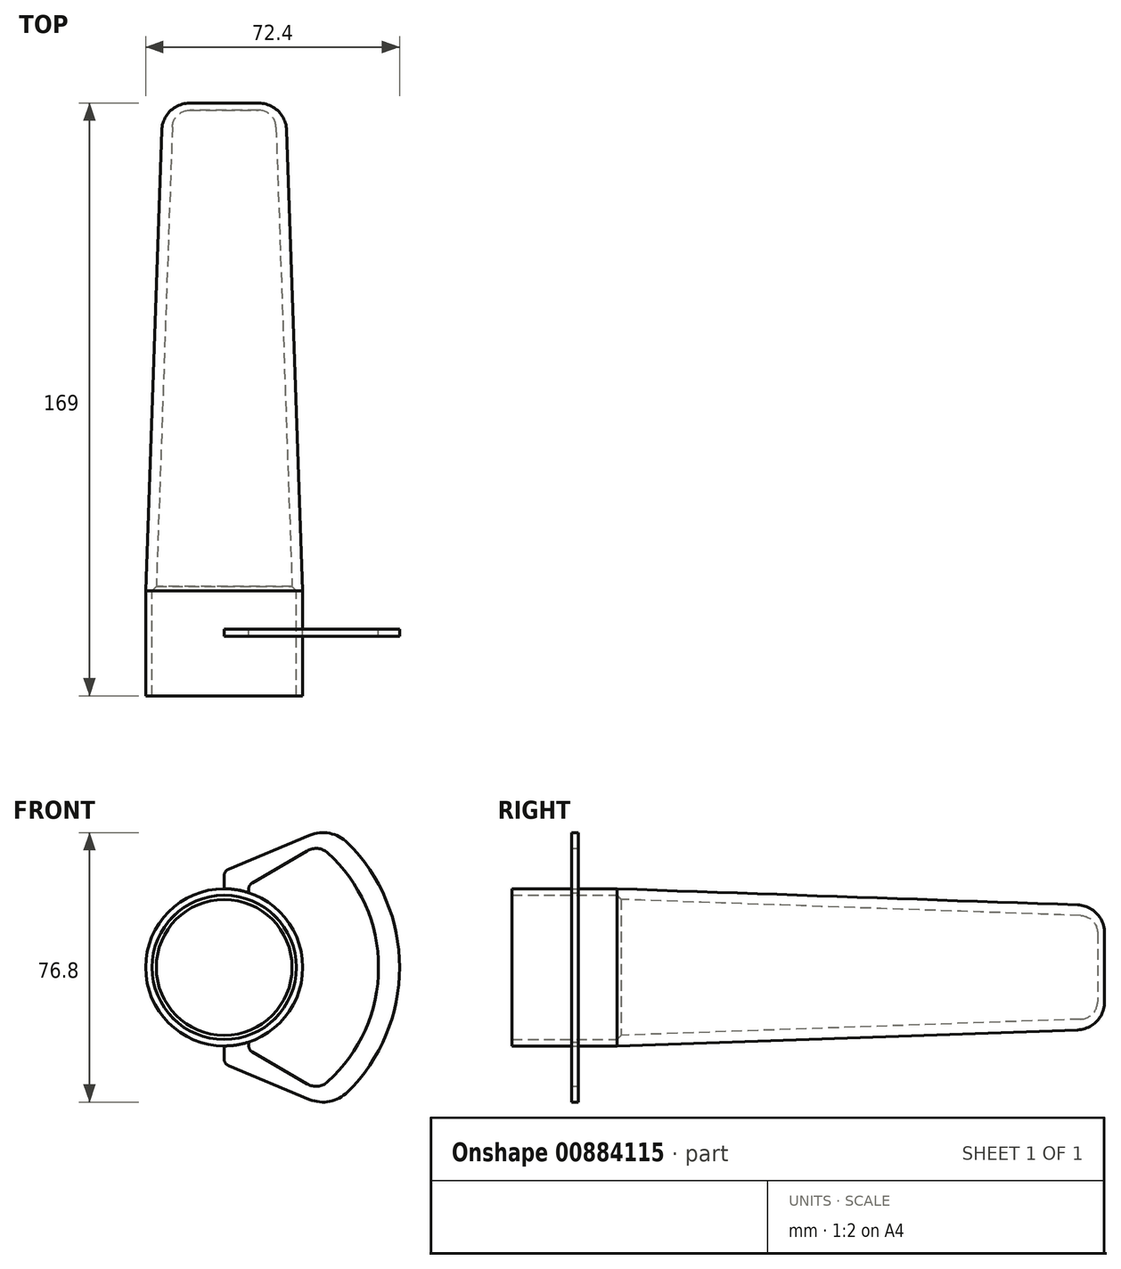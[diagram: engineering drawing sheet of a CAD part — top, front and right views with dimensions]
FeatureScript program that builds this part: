
annotation { "Feature Type Name" : "Feature", "Feature Type Description" : "" }
export const myFeature = defineFeature(function(context is Context, id is Id, definition is map)
    precondition{}
    {
        {
            var Q0;
            Q0=qCreatedBy(makeId("Front.planeOp"),FACE);
            var sketch = newSketch(context, id + "F0", { "sketchPlane" : qUnion([Q0])});
            skCircle(sketch, "E0", {"center": v(-13.8, 50.8) * mm, "radius": 22.4 * mm});
            skCircle(sketch, "E1", {"center": v(-13.8, 50.8) * mm, "radius": 20.57 * mm});
            skLineSegment(sketch, "E2", {"start": v(-12.57, 22.79) * mm, "end": v(10.52, 13.17) * mm});
            skLineSegment(sketch, "E3", {"start": v(-12.57, 78.81) * mm, "end": v(10.52, 88.43) * mm});
            skLineSegment(sketch, "E4", {"start": v(9.84, 17.57) * mm, "end": v(-5.8, 26.72) * mm});
            skLineSegment(sketch, "E5", {"start": v(-5.8, 74.88) * mm, "end": v(9.84, 84.03) * mm});
            skArc(sketch, "E6", {"start": v(21.4, 15.3) * mm, "mid": v(36.2, 50.8) * mm, "end": v(21.4, 86.3) * mm});
            skArc(sketch, "E7", {"start": v(15.72, 18.17) * mm, "mid": v(30.2, 50.8) * mm, "end": v(15.72, 83.42) * mm});
            skLineSegment(sketch, "E8", {"start": v(-13.8, 73.2) * mm, "end": v(-13.8, 76.97) * mm});
            skLineSegment(sketch, "E9", {"start": v(-6.8, 73.15) * mm, "end": v(-6.8, 72.08) * mm});
            skLineSegment(sketch, "E10", {"start": v(-6.8, 29.52) * mm, "end": v(-6.8, 28.45) * mm});
            skLineSegment(sketch, "E11", {"start": v(-13.8, 24.63) * mm, "end": v(-13.8, 28.4) * mm});
            skArc(sketch, "E12", {"start": v(15.72, 83.42) * mm, "mid": v(12.88, 84.69) * mm, "end": v(9.84, 84.03) * mm});
            skArc(sketch, "E13", {"start": v(9.84, 17.57) * mm, "mid": v(12.88, 16.9) * mm, "end": v(15.72, 18.17) * mm});
            skArc(sketch, "E14", {"start": v(21.4, 86.3) * mm, "mid": v(16.29, 89.02) * mm, "end": v(10.52, 88.43) * mm});
            skArc(sketch, "E15", {"start": v(10.52, 13.17) * mm, "mid": v(16.29, 12.58) * mm, "end": v(21.4, 15.3) * mm});
            skArc(sketch, "E16", {"start": v(-6.8, 28.45) * mm, "mid": v(-6.53, 27.45) * mm, "end": v(-5.8, 26.72) * mm});
            skArc(sketch, "E17", {"start": v(-13.8, 24.63) * mm, "mid": v(-13.46, 23.52) * mm, "end": v(-12.57, 22.79) * mm});
            skArc(sketch, "E18", {"start": v(-12.57, 78.81) * mm, "mid": v(-13.46, 78.07) * mm, "end": v(-13.8, 76.97) * mm});
            skArc(sketch, "E19", {"start": v(-5.8, 74.88) * mm, "mid": v(-6.53, 74.15) * mm, "end": v(-6.8, 73.15) * mm});
            skLineSegment(sketch, "E20", {"start": v(8.6, 40.3) * mm, "end": v(8.6, 70.3) * mm});
            skLineSegment(sketch, "E21", {"start": v(8.6, 70.3) * mm, "end": v(6.78, 70.3) * mm});
            skLineSegment(sketch, "E22", {"start": v(-5.78, -89.2) * mm, "end": v(-13.8, -89.2) * mm});
            skLineSegment(sketch, "E23", {"start": v(2.21, -81.62) * mm, "end": v(8.6, 40.3) * mm});
            skLineSegment(sketch, "E24", {"start": v(6.78, 41.48) * mm, "end": v(5.6, 40.3) * mm});
            skLineSegment(sketch, "E25", {"start": v(-5.83, -87.2) * mm, "end": v(-13.8, -87.2) * mm});
            skArc(sketch, "E26", {"start": v(-5.83, -87.2) * mm, "mid": v(-2.39, -85.83) * mm, "end": v(-0.84, -82.46) * mm});
            skLineSegment(sketch, "E27", {"start": v(5.6, 40.3) * mm, "end": v(-0.84, -82.46) * mm});
            skArc(sketch, "E28", {"start": v(-5.78, -89.2) * mm, "mid": v(-0.27, -87) * mm, "end": v(2.21, -81.62) * mm});
            skLineSegment(sketch, "E29", {"start": v(6.78, 70.3) * mm, "end": v(6.78, 41.48) * mm});
            skSolve(sketch);
        }
        {
            var Q0;
            Q0=qCreatedBy(makeId("Top.planeOp"),FACE);
            var Q1;
            Q1=sQuery(id+"F0.wireOp",VERTEX,"E0.center");
            cPlane(context, id + "F1", {"entities" : qUnion([Q0, Q1]), "cplaneType" : CPlaneType.PLANE_POINT, "offset" : 25 * mm, "width" : 150 * mm, "height" : 150 * mm});
        }
        {
            var Q0;
            Q0=qCreatedBy(makeId("Front.planeOp"),FACE);
            var sketch = newSketch(context, id + "F2", { "sketchPlane" : qUnion([Q0])});
            skCircle(sketch, "E30.0", {"center": v(-13.8, 50.8) * mm, "radius": 20.57 * mm});
            skArc(sketch, "E31.0", {"start": v(-6.8, 72.08) * mm, "mid": v(8.6, 50.8) * mm, "end": v(-6.8, 29.52) * mm});
            skLineSegment(sketch, "E31.1", {"start": v(-13.8, 73.2) * mm, "end": v(-13.8, 76.97) * mm});
            skArc(sketch, "E31.2", {"start": v(-12.57, 78.81) * mm, "mid": v(-13.46, 78.07) * mm, "end": v(-13.8, 76.97) * mm});
            skLineSegment(sketch, "E31.3", {"start": v(-12.57, 78.81) * mm, "end": v(10.52, 88.43) * mm});
            skLineSegment(sketch, "E31.4", {"start": v(-5.8, 74.88) * mm, "end": v(9.84, 84.03) * mm});
            skArc(sketch, "E32.0", {"start": v(-5.8, 74.88) * mm, "mid": v(-6.53, 74.15) * mm, "end": v(-6.8, 73.15) * mm});
            skLineSegment(sketch, "E33.0", {"start": v(-6.8, 73.15) * mm, "end": v(-6.8, 72.08) * mm});
            skArc(sketch, "E34.0", {"start": v(15.72, 83.42) * mm, "mid": v(12.88, 84.69) * mm, "end": v(9.84, 84.03) * mm});
            skArc(sketch, "E35.0", {"start": v(21.4, 86.3) * mm, "mid": v(16.29, 89.02) * mm, "end": v(10.52, 88.43) * mm});
            skArc(sketch, "E36.0", {"start": v(21.4, 15.3) * mm, "mid": v(36.2, 50.8) * mm, "end": v(21.4, 86.3) * mm});
            skArc(sketch, "E37.0", {"start": v(15.72, 18.17) * mm, "mid": v(30.2, 50.8) * mm, "end": v(15.72, 83.42) * mm});
            skArc(sketch, "E38.0", {"start": v(10.52, 13.17) * mm, "mid": v(16.29, 12.58) * mm, "end": v(21.4, 15.3) * mm});
            skArc(sketch, "E39.0", {"start": v(9.84, 17.57) * mm, "mid": v(12.88, 16.9) * mm, "end": v(15.72, 18.17) * mm});
            skLineSegment(sketch, "E40.0", {"start": v(9.84, 17.57) * mm, "end": v(-5.8, 26.72) * mm});
            skLineSegment(sketch, "E41.0", {"start": v(-12.57, 22.79) * mm, "end": v(10.52, 13.17) * mm});
            skArc(sketch, "E42.0", {"start": v(-6.8, 28.45) * mm, "mid": v(-6.53, 27.45) * mm, "end": v(-5.8, 26.72) * mm});
            skArc(sketch, "E43.0", {"start": v(-13.8, 24.63) * mm, "mid": v(-13.46, 23.52) * mm, "end": v(-12.57, 22.79) * mm});
            skLineSegment(sketch, "E44.0", {"start": v(-13.8, 24.63) * mm, "end": v(-13.8, 28.4) * mm});
            skPoint(sketch, "E45.0", {"position": v(-6.8, 28.98) * mm});
            skLineSegment(sketch, "E46.0", {"start": v(-6.8, 29.52) * mm, "end": v(-6.8, 28.45) * mm});
            skArc(sketch, "E47.trimOffspring", {"start": v(-13.8, 28.4) * mm, "mid": v(-36.2, 50.8) * mm, "end": v(-13.8, 73.2) * mm});
            skSolve(sketch);
        }
        {
            var Q0;
            Q0 = qSketchRegion(id + "F2", true);
            extrude(context, id + "F3", {"entities" : qUnion([Q0]), "depth" : 2 * mm, "offsetDistance" : 25 * mm});
        }
        {
            var Q0;
            Q0=makeQuery(id+"F3.opExtrude","CAP_FACE",FACE,{"disambiguationData":[OSD([sQuery(id+"F2.wireOp",EDGE,"E30.0"),sQuery(id+"F2.wireOp",EDGE,"E31.0"),sQuery(id+"F2.wireOp",EDGE,"E31.1"),sQuery(id+"F2.wireOp",EDGE,"E31.2"),sQuery(id+"F2.wireOp",EDGE,"E31.3"),sQuery(id+"F2.wireOp",EDGE,"E31.4"),sQuery(id+"F2.wireOp",EDGE,"E32.0"),sQuery(id+"F2.wireOp",EDGE,"E33.0"),sQuery(id+"F2.wireOp",EDGE,"E34.0"),sQuery(id+"F2.wireOp",EDGE,"E35.0"),sQuery(id+"F2.wireOp",EDGE,"E36.0"),sQuery(id+"F2.wireOp",EDGE,"E37.0"),sQuery(id+"F2.wireOp",EDGE,"E38.0"),sQuery(id+"F2.wireOp",EDGE,"E39.0"),sQuery(id+"F2.wireOp",EDGE,"E40.0"),sQuery(id+"F2.wireOp",EDGE,"E41.0"),sQuery(id+"F2.wireOp",EDGE,"E42.0"),sQuery(id+"F2.wireOp",EDGE,"E43.0"),sQuery(id+"F2.wireOp",EDGE,"E44.0"),sQuery(id+"F2.wireOp",EDGE,"E46.0"),sQuery(id+"F2.wireOp",EDGE,"E47.trimOffspring")])],"isStart":false});
            var sketch = newSketch(context, id + "F4", { "sketchPlane" : qUnion([Q0])});
            skCircle(sketch, "E48.0", {"center": v(-13.8, 50.8) * mm, "radius": 20.57 * mm});
            skCircle(sketch, "E49.0", {"center": v(-13.8, 50.8) * mm, "radius": 22.4 * mm});
            skSolve(sketch);
        }
        {
            var Q0;
            Q0 = qSketchRegion(id + "F4", true);
            extrude(context, id + "F5", {"entities" : qUnion([Q0]), "operationType" : NewBodyOperationType.ADD, "depth" : 17 * mm, "offsetDistance" : 25 * mm});
        }
        {
            var Q0;
            Q0=makeQuery(id+"F5.opExtrude","CAP_FACE",FACE,{"disambiguationData":[OSD([sQuery(id+"F4.wireOp",EDGE,"E48.0"),sQuery(id+"F4.wireOp",EDGE,"E49.0")])],"isStart":false});
            extrude(context, id + "F6", {"entities" : qUnion([Q0]), "operationType" : NewBodyOperationType.ADD, "oppositeDirection" : true, "depth" : 30 * mm, "offsetDistance" : 25 * mm});
        }
        {
            var Q0;
            Q0=qCreatedBy(id+"F1.planeOp",FACE);
            var sketch = newSketch(context, id + "F7", { "sketchPlane" : qUnion([Q0])});
            skLineSegment(sketch, "E50", {"start": v(8.6, 11) * mm, "end": v(4.02, 142.28) * mm});
            skLineSegment(sketch, "E51", {"start": v(-3.98, 150) * mm, "end": v(-13.8, 150) * mm});
            skLineSegment(sketch, "E52", {"start": v(-13.8, 150) * mm, "end": v(-13.8, 148) * mm});
            skLineSegment(sketch, "E53", {"start": v(-13.8, 148) * mm, "end": v(-4.01, 148) * mm});
            skLineSegment(sketch, "E54", {"start": v(0.98, 143.17) * mm, "end": v(5.56, 12.2) * mm});
            skLineSegment(sketch, "E55", {"start": v(5.56, 12.2) * mm, "end": v(6.76, 11) * mm});
            skLineSegment(sketch, "E56", {"start": v(6.76, 11) * mm, "end": v(8.6, 11) * mm});
            skPoint(sketch, "E57.visualSharp", {"position": v(0.81, 148) * mm});
            skArc(sketch, "E57.filletArc", {"start": v(0.98, 143.17) * mm, "mid": v(-0.54, 146.6) * mm, "end": v(-4.01, 148) * mm});
            skPoint(sketch, "E58.visualSharp", {"position": v(3.75, 150) * mm});
            skArc(sketch, "E58.filletArc", {"start": v(4.02, 142.28) * mm, "mid": v(1.58, 147.75) * mm, "end": v(-3.98, 150) * mm});
            skSolve(sketch);
        }
        {
            var Q0;
            Q0=makeQuery(id+"F7.imprint","IMPRINT",FACE,{"disambiguationData":[TD([[makeQuery(id+"F7.imprint","IMPRINT",EDGE,{"derivedFrom":sQuery(id+"F7.wireOp",EDGE,"E50")}),1.0]])]});
            var Q1;
            Q1=sQuery(id+"F7.wireOp",EDGE,"E52");
            revolve(context, id + "F8", {"operationType" : NewBodyOperationType.ADD, "surfaceOperationType" : NewSurfaceOperationType.NEW, "entities" : qUnion([Q0]), "axis" : qUnion([Q1]), "revolveType" : RevolveType.FULL});
        }
    });
